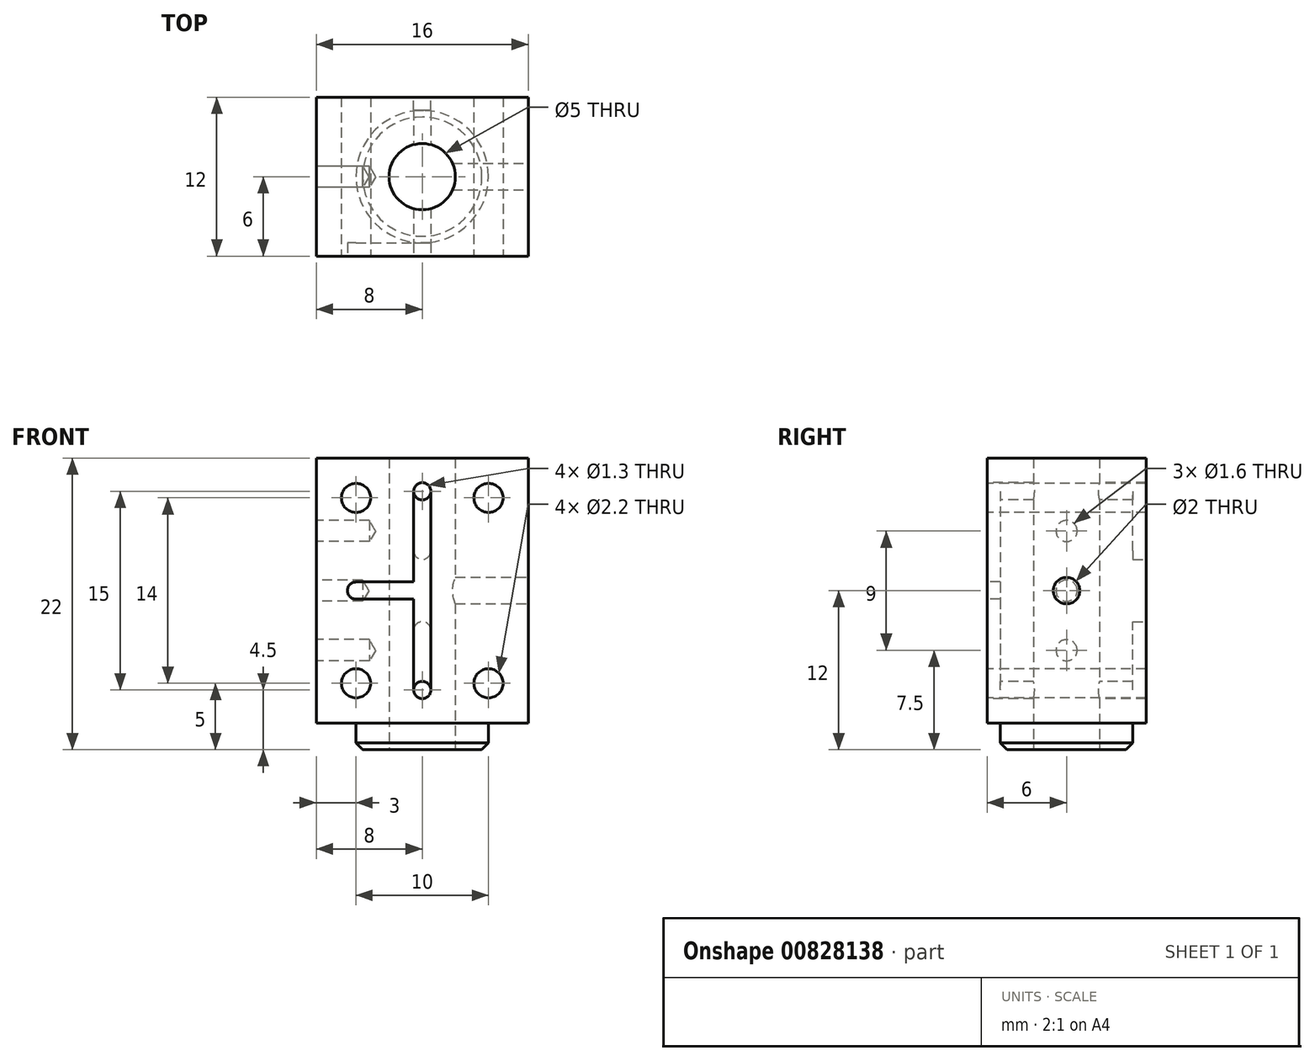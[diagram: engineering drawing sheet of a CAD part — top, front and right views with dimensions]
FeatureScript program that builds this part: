
annotation { "Feature Type Name" : "Feature", "Feature Type Description" : "" }
export const myFeature = defineFeature(function(context is Context, id is Id, definition is map)
    precondition{}
    {
        {
            var Q0;
            Q0=qCreatedBy(makeId("Front.planeOp"),FACE);
            var sketch = newSketch(context, id + "F0", { "sketchPlane" : qUnion([Q0])});
            skLineSegment(sketch, "E0.bottom", {"start": v(0, 0) * mm, "end": v(16, 0) * mm});
            skLineSegment(sketch, "E0.top", {"start": v(0, -20) * mm, "end": v(16, -20) * mm});
            skLineSegment(sketch, "E0.left", {"start": v(0, 0) * mm, "end": v(0, -20) * mm});
            skLineSegment(sketch, "E0.right", {"start": v(16, 0) * mm, "end": v(16, -20) * mm});
            skSolve(sketch);
        }
        {
            var Q0;
            Q0 = qSketchRegion(id + "F0", true);
            extrude(context, id + "F1", {"entities" : qUnion([Q0]), "depth" : 12 * mm, "offsetDistance" : 25 * mm});
        }
        {
            var Q0;
            Q0=makeQuery(id+"F1.opExtrude","SWEPT_FACE",FACE,{"disambiguationData":[OSD([sQuery(id+"F0.wireOp",EDGE,"E0.top")])]});
            var sketch = newSketch(context, id + "F2", { "sketchPlane" : qUnion([Q0])});
            skCircle(sketch, "E1", {"center": v(8, 6) * mm, "radius": 5 * mm});
            skPoint(sketch, "E1.centerSnap0", {"position": v(16, 6) * mm});
            skPoint(sketch, "E1.centerSnap1", {"position": v(8, 12) * mm});
            skSolve(sketch);
        }
        {
            var Q0;
            Q0 = qSketchRegion(id + "F2", true);
            extrude(context, id + "F3", {"entities" : qUnion([Q0]), "operationType" : NewBodyOperationType.ADD, "depth" : 2 * mm, "offsetDistance" : 25 * mm});
        }
        {
            var Q0;
            Q0=makeQuery(id+"F3.opExtrude","CAP_EDGE",EDGE,{"disambiguationData":[OSD([sQuery(id+"F2.wireOp",EDGE,"E1")])],"isStart":false});
            chamfer(context, id + "F4", {"entities" : qUnion([Q0]), "width" : 0.5 * mm, "tangentPropagation" : true});
        }
        {
            var Q0;
            Q0=makeQuery(id+"F3.opExtrude","CAP_FACE",FACE,{"disambiguationData":[OSD([sQuery(id+"F2.wireOp",EDGE,"E1")])],"isStart":false});
            var sketch = newSketch(context, id + "F5", { "sketchPlane" : qUnion([Q0])});
            skCircle(sketch, "E2", {"center": v(8, 6) * mm, "radius": 2.5 * mm});
            skSolve(sketch);
        }
        {
            var Q0;
            Q0=makeQuery(id+"F1.opExtrude","SWEPT_FACE",FACE,{"disambiguationData":[OSD([sQuery(id+"F0.wireOp",EDGE,"E0.top")])]});
            var Q1;
            Q1=makeQuery(id+"F1.opExtrude","SWEPT_FACE",FACE,{"disambiguationData":[OSD([sQuery(id+"F0.wireOp",EDGE,"E0.bottom")])]});
            cPlane(context, id + "F6", {"entities" : qUnion([Q0, Q1]), "cplaneType" : CPlaneType.MID_PLANE, "offset" : 25 * mm, "width" : 150 * mm, "height" : 150 * mm});
        }
        {
            var Q0;
            Q0 = qSketchRegion(id + "F5", true);
            extrude(context, id + "F7", {"entities" : qUnion([Q0]), "operationType" : NewBodyOperationType.REMOVE, "endBound" : BoundingType.THROUGH_ALL, "oppositeDirection" : true, "depth" : 25 * mm, "offsetDistance" : 25 * mm});
        }
        {
            var Q0;
            Q0=makeQuery(id+"F1.opExtrude","CAP_FACE",FACE,{"disambiguationData":[OSD([sQuery(id+"F0.wireOp",EDGE,"E0.bottom"),sQuery(id+"F0.wireOp",EDGE,"E0.top"),sQuery(id+"F0.wireOp",EDGE,"E0.left"),sQuery(id+"F0.wireOp",EDGE,"E0.right")])],"isStart":false});
            var sketch = newSketch(context, id + "F8", { "sketchPlane" : qUnion([Q0])});
            skLineSegment(sketch, "E3", {"start": v(8, 0) * mm, "end": v(8, -20) * mm, "construction": true});
            skLineSegment(sketch, "E4", {"start": v(0, -10) * mm, "end": v(16, -10) * mm, "construction": true});
            skArc(sketch, "E5", {"start": v(8.65, -2.5) * mm, "mid": v(8, -1.85) * mm, "end": v(7.35, -2.5) * mm});
            skArc(sketch, "E6", {"start": v(7.35, -17.5) * mm, "mid": v(8, -18.15) * mm, "end": v(8.65, -17.5) * mm});
            skArc(sketch, "E7", {"start": v(3, -9.35) * mm, "mid": v(2.35, -10) * mm, "end": v(3, -10.65) * mm});
            skLineSegment(sketch, "E8", {"start": v(7.35, -2.5) * mm, "end": v(7.35, -9.35) * mm});
            skLineSegment(sketch, "E9", {"start": v(8.65, -2.5) * mm, "end": v(8.65, -17.5) * mm});
            skLineSegment(sketch, "E10", {"start": v(3, -10.65) * mm, "end": v(7.35, -10.65) * mm});
            skLineSegment(sketch, "E11", {"start": v(3, -9.35) * mm, "end": v(7.35, -9.35) * mm});
            skLineSegment(sketch, "E12.trimOffspring", {"start": v(7.35, -10.65) * mm, "end": v(7.35, -17.5) * mm});
            skSolve(sketch);
        }
        {
            var Q0;
            Q0 = qSketchRegion(id + "F8", true);
            extrude(context, id + "F9", {"entities" : qUnion([Q0]), "operationType" : NewBodyOperationType.REMOVE, "oppositeDirection" : true, "depth" : 1 * mm, "offsetDistance" : 25 * mm});
        }
        {
            var Q0;
            Q0=makeQuery(id+"F1.opExtrude","CAP_FACE",FACE,{"disambiguationData":[OSD([sQuery(id+"F0.wireOp",EDGE,"E0.bottom"),sQuery(id+"F0.wireOp",EDGE,"E0.top"),sQuery(id+"F0.wireOp",EDGE,"E0.left"),sQuery(id+"F0.wireOp",EDGE,"E0.right")])],"isStart":false});
            var sketch = newSketch(context, id + "F10", { "sketchPlane" : qUnion([Q0])});
            skPoint(sketch, "E13", {"position": v(3, -3) * mm});
            skPoint(sketch, "E14", {"position": v(13, -3) * mm});
            skPoint(sketch, "E15", {"position": v(13, -17) * mm});
            skPoint(sketch, "E16", {"position": v(3, -17) * mm});
            skSolve(sketch);
        }
        {
            var Q0;
            Q0=sQuery(id+"F10.wireOp",VERTEX,"E13");
            var Q1;
            Q1=sQuery(id+"F10.wireOp",VERTEX,"E14");
            var Q2;
            Q2=sQuery(id+"F10.wireOp",VERTEX,"E15");
            var Q3;
            Q3=sQuery(id+"F10.wireOp",VERTEX,"E16");
            var Q4;
            Q4=makeQuery(id+"F1.opExtrude","SWEPT_BODY",BODY,{"disambiguationData":[OSD([sQuery(id+"F0.wireOp",EDGE,"E0.bottom"),sQuery(id+"F0.wireOp",EDGE,"E0.top"),sQuery(id+"F0.wireOp",EDGE,"E0.left"),sQuery(id+"F0.wireOp",EDGE,"E0.right")])]});
            hole(context, id + "F11", {"style" : HoleStyle.SIMPLE, "endStyle" : HoleEndStyle.THROUGH, "standardTappedOrClearance" : lookupTablePath({ "standard" : "ISO", "size" : "2.2", "type" : "Drilled" }), "standardBlindInLast" : lookupTablePath({ "standard" : "ISO", "size" : "2.2", "type" : "Drilled" }), "holeDiameter" : 2.2 * mm, "majorDiameter" : 5 * mm, "isTappedThrough" : true, "tappedDepth" : 7.3 * mm, "tapClearance" : 3, "locations" : qUnion([Q0, Q1, Q2, Q3]), "scope" : qUnion([Q4])});
        }
        {
            var Q0;
            Q0=makeQuery(id+"F1.opExtrude","CAP_FACE",FACE,{"disambiguationData":[OSD([sQuery(id+"F0.wireOp",EDGE,"E0.bottom"),sQuery(id+"F0.wireOp",EDGE,"E0.top"),sQuery(id+"F0.wireOp",EDGE,"E0.left"),sQuery(id+"F0.wireOp",EDGE,"E0.right")])],"isStart":false});
            var sketch = newSketch(context, id + "F12", { "sketchPlane" : qUnion([Q0])});
            skPoint(sketch, "E17", {"position": v(8, -2.5) * mm});
            skPoint(sketch, "E18", {"position": v(8, -17.5) * mm});
            skPoint(sketch, "E19", {"position": v(8, -7) * mm});
            skPoint(sketch, "E20", {"position": v(8, -13) * mm});
            skSolve(sketch);
        }
        {
            var Q0;
            Q0=sQuery(id+"F12.wireOp",VERTEX,"E17");
            var Q1;
            Q1=sQuery(id+"F12.wireOp",VERTEX,"E18");
            var Q2;
            Q2=makeQuery(id+"F1.opExtrude","SWEPT_BODY",BODY,{"disambiguationData":[OSD([sQuery(id+"F0.wireOp",EDGE,"E0.bottom"),sQuery(id+"F0.wireOp",EDGE,"E0.top"),sQuery(id+"F0.wireOp",EDGE,"E0.left"),sQuery(id+"F0.wireOp",EDGE,"E0.right")])]});
            hole(context, id + "F13", {"style" : HoleStyle.SIMPLE, "endStyle" : HoleEndStyle.THROUGH, "standardTappedOrClearance" : lookupTablePath({ "standard" : "ISO", "size" : "1.3", "type" : "Drilled" }), "standardBlindInLast" : lookupTablePath({ "standard" : "ISO", "size" : "1.3", "type" : "Drilled" }), "holeDiameter" : 1.3 * mm, "majorDiameter" : 5 * mm, "isTappedThrough" : true, "tappedDepth" : 7.3 * mm, "tapClearance" : 3, "locations" : qUnion([Q0, Q1]), "scope" : qUnion([Q2])});
        }
        {
            var Q0;
            Q0=makeQuery(id+"F1.opExtrude","CAP_FACE",FACE,{"disambiguationData":[OSD([sQuery(id+"F0.wireOp",EDGE,"E0.bottom"),sQuery(id+"F0.wireOp",EDGE,"E0.top"),sQuery(id+"F0.wireOp",EDGE,"E0.left"),sQuery(id+"F0.wireOp",EDGE,"E0.right")])],"isStart":true});
            var sketch = newSketch(context, id + "F14", { "sketchPlane" : qUnion([Q0])});
            skPoint(sketch, "E21", {"position": v(-8, -13) * mm});
            skPoint(sketch, "E22", {"position": v(-8, -7) * mm});
            skArc(sketch, "E23", {"start": v(-8.65, -7) * mm, "mid": v(-8, -7.65) * mm, "end": v(-7.35, -7) * mm});
            skArc(sketch, "E24", {"start": v(-7.35, -13) * mm, "mid": v(-8, -12.35) * mm, "end": v(-8.65, -13) * mm});
            skArc(sketch, "E25.0", {"start": v(-7.35, -2.5) * mm, "mid": v(-8, -1.85) * mm, "end": v(-8.65, -2.5) * mm});
            skLineSegment(sketch, "E26", {"start": v(-7.35, -7) * mm, "end": v(-7.35, -2.5) * mm});
            skLineSegment(sketch, "E27", {"start": v(-8.65, -7) * mm, "end": v(-8.65, -2.5) * mm});
            skArc(sketch, "E28.0", {"start": v(-8.65, -17.5) * mm, "mid": v(-8, -18.15) * mm, "end": v(-7.35, -17.5) * mm});
            skLineSegment(sketch, "E29", {"start": v(-7.35, -17.5) * mm, "end": v(-7.35, -13) * mm});
            skLineSegment(sketch, "E30", {"start": v(-8.65, -17.5) * mm, "end": v(-8.65, -13) * mm});
            skSolve(sketch);
        }
        {
            var Q0;
            Q0 = qSketchRegion(id + "F14", true);
            extrude(context, id + "F15", {"entities" : qUnion([Q0]), "operationType" : NewBodyOperationType.REMOVE, "oppositeDirection" : true, "depth" : 1 * mm, "offsetDistance" : 25 * mm});
        }
        {
            var Q0;
            Q0=makeQuery(id+"F1.opExtrude","SWEPT_FACE",FACE,{"disambiguationData":[OSD([sQuery(id+"F0.wireOp",EDGE,"E0.left")])]});
            var sketch = newSketch(context, id + "F16", { "sketchPlane" : qUnion([Q0])});
            skLineSegment(sketch, "E31", {"start": v(6, -20) * mm, "end": v(6, 0) * mm, "construction": true});
            skLineSegment(sketch, "E32", {"start": v(0, -10) * mm, "end": v(12, -10) * mm, "construction": true});
            skPoint(sketch, "E33", {"position": v(6, -14.5) * mm});
            skPoint(sketch, "E34", {"position": v(6, -10) * mm});
            skPoint(sketch, "E35", {"position": v(6, -5.5) * mm});
            skSolve(sketch);
        }
        {
            var Q0;
            Q0=sQuery(id+"F16.wireOp",VERTEX,"E33");
            var Q1;
            Q1=sQuery(id+"F16.wireOp",VERTEX,"E35");
            var Q2;
            Q2=makeQuery(id+"F1.opExtrude","SWEPT_BODY",BODY,{"disambiguationData":[OSD([sQuery(id+"F0.wireOp",EDGE,"E0.bottom"),sQuery(id+"F0.wireOp",EDGE,"E0.top"),sQuery(id+"F0.wireOp",EDGE,"E0.left"),sQuery(id+"F0.wireOp",EDGE,"E0.right")])]});
            hole(context, id + "F17", {"style" : HoleStyle.SIMPLE, "endStyle" : HoleEndStyle.BLIND, "standardTappedOrClearance" : lookupTablePath({ "standard" : "ISO", "size" : "1.6", "type" : "Drilled" }), "standardBlindInLast" : lookupTablePath({ "standard" : "ISO", "size" : "1.6", "type" : "Drilled" }), "holeDiameter" : 1.6 * mm, "majorDiameter" : 5 * mm, "holeDepth" : 4 * mm, "isTappedThrough" : true, "tappedDepth" : 7.3 * mm, "tapClearance" : 3, "locations" : qUnion([Q0, Q1]), "scope" : qUnion([Q2])});
        }
        {
            var Q0;
            Q0=makeQuery(id+"F1.opExtrude","SWEPT_FACE",FACE,{"disambiguationData":[OSD([sQuery(id+"F0.wireOp",EDGE,"E0.left")])]});
            var Q1;
            Q1=makeQuery(id+"F1.opExtrude","SWEPT_FACE",FACE,{"disambiguationData":[OSD([sQuery(id+"F0.wireOp",EDGE,"E0.right")])]});
            cPlane(context, id + "F18", {"entities" : qUnion([Q0, Q1]), "cplaneType" : CPlaneType.MID_PLANE, "offset" : 25 * mm, "width" : 150 * mm, "height" : 150 * mm});
        }
        {
            var Q0;
            Q0=sQuery(id+"F16.wireOp",VERTEX,"E34");
            var Q1;
            Q1=makeQuery(id+"F1.opExtrude","SWEPT_BODY",BODY,{"disambiguationData":[OSD([sQuery(id+"F0.wireOp",EDGE,"E0.bottom"),sQuery(id+"F0.wireOp",EDGE,"E0.top"),sQuery(id+"F0.wireOp",EDGE,"E0.left"),sQuery(id+"F0.wireOp",EDGE,"E0.right")])]});
            hole(context, id + "F19", {"style" : HoleStyle.SIMPLE, "endStyle" : HoleEndStyle.BLIND, "standardTappedOrClearance" : lookupTablePath({ "standard" : "ISO", "size" : "1.6", "type" : "Drilled" }), "standardBlindInLast" : lookupTablePath({ "standard" : "ISO", "size" : "1.6", "type" : "Drilled" }), "holeDiameter" : 1.6 * mm, "majorDiameter" : 5 * mm, "holeDepth" : 3.5 * mm, "isTappedThrough" : true, "tappedDepth" : 7.3 * mm, "tapClearance" : 3, "locations" : qUnion([Q0]), "scope" : qUnion([Q1])});
        }
        {
            var Q0;
            Q0=makeQuery(id+"F1.opExtrude","SWEPT_FACE",FACE,{"disambiguationData":[OSD([sQuery(id+"F0.wireOp",EDGE,"E0.right")])]});
            var sketch = newSketch(context, id + "F20", { "sketchPlane" : qUnion([Q0])});
            skLineSegment(sketch, "E36", {"start": v(-12, -10) * mm, "end": v(0, -10) * mm});
            skPoint(sketch, "E37", {"position": v(-6, -10) * mm});
            skSolve(sketch);
        }
        {
            var Q0;
            Q0=sQuery(id+"F20.wireOp",VERTEX,"E37");
            var Q1;
            Q1=makeQuery(id+"F1.opExtrude","SWEPT_BODY",BODY,{"disambiguationData":[OSD([sQuery(id+"F0.wireOp",EDGE,"E0.bottom"),sQuery(id+"F0.wireOp",EDGE,"E0.top"),sQuery(id+"F0.wireOp",EDGE,"E0.left"),sQuery(id+"F0.wireOp",EDGE,"E0.right")])]});
            hole(context, id + "F21", {"style" : HoleStyle.SIMPLE, "endStyle" : HoleEndStyle.BLIND, "holeDiameter" : 2 * mm, "majorDiameter" : 5 * mm, "holeDepth" : 8 * mm, "isTappedThrough" : true, "tappedDepth" : 7.3 * mm, "tapClearance" : 3, "locations" : qUnion([Q0]), "scope" : qUnion([Q1])});
        }
    });
